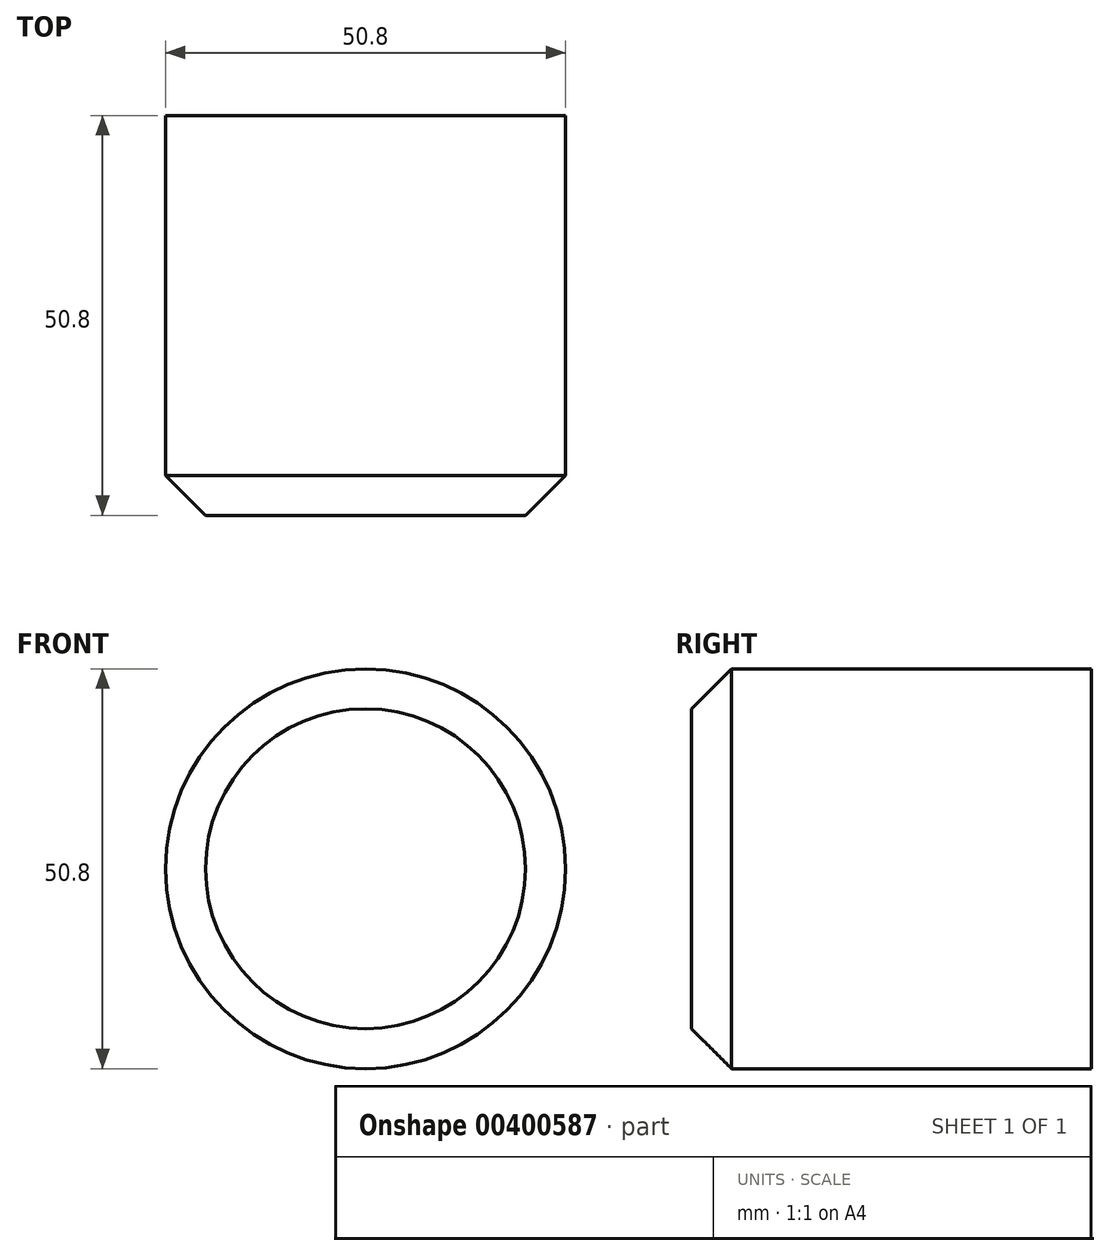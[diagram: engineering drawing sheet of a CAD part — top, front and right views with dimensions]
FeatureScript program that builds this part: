
annotation { "Feature Type Name" : "Feature", "Feature Type Description" : "" }
export const myFeature = defineFeature(function(context is Context, id is Id, definition is map)
    precondition{}
    {
        {
            var Q0;
            Q0=qCreatedBy(makeId("Front.planeOp"),FACE);
            var sketch = newSketch(context, id + "F0", { "sketchPlane" : qUnion([Q0])});
            skCircle(sketch, "E0", {"center": v(38.05, 35.53) * mm, "radius": 25.4 * mm});
            skSolve(sketch);
        }
        {
            var Q0;
            Q0=makeQuery(id+"F0.imprint","IMPRINT",FACE,{"disambiguationData":[TD([[makeQuery(id+"F0.imprint","IMPRINT",EDGE,{"derivedFrom":sQuery(id+"F0.wireOp",EDGE,"E0")}),1.0]])]});
            extrude(context, id + "F1", {"entities" : qUnion([Q0]), "depth" : 50.8 * mm});
        }
        {
            var Q0;
            Q0=makeQuery(id+"F1.opExtrude","CAP_FACE",FACE,{"disambiguationData":[OSD([sQuery(id+"F0.wireOp",EDGE,"E0")])],"isStart":false});
            chamfer(context, id + "F2", {"entities" : qUnion([Q0]), "width" : 5.08 * mm, "tangentPropagation" : true});
        }
    });
